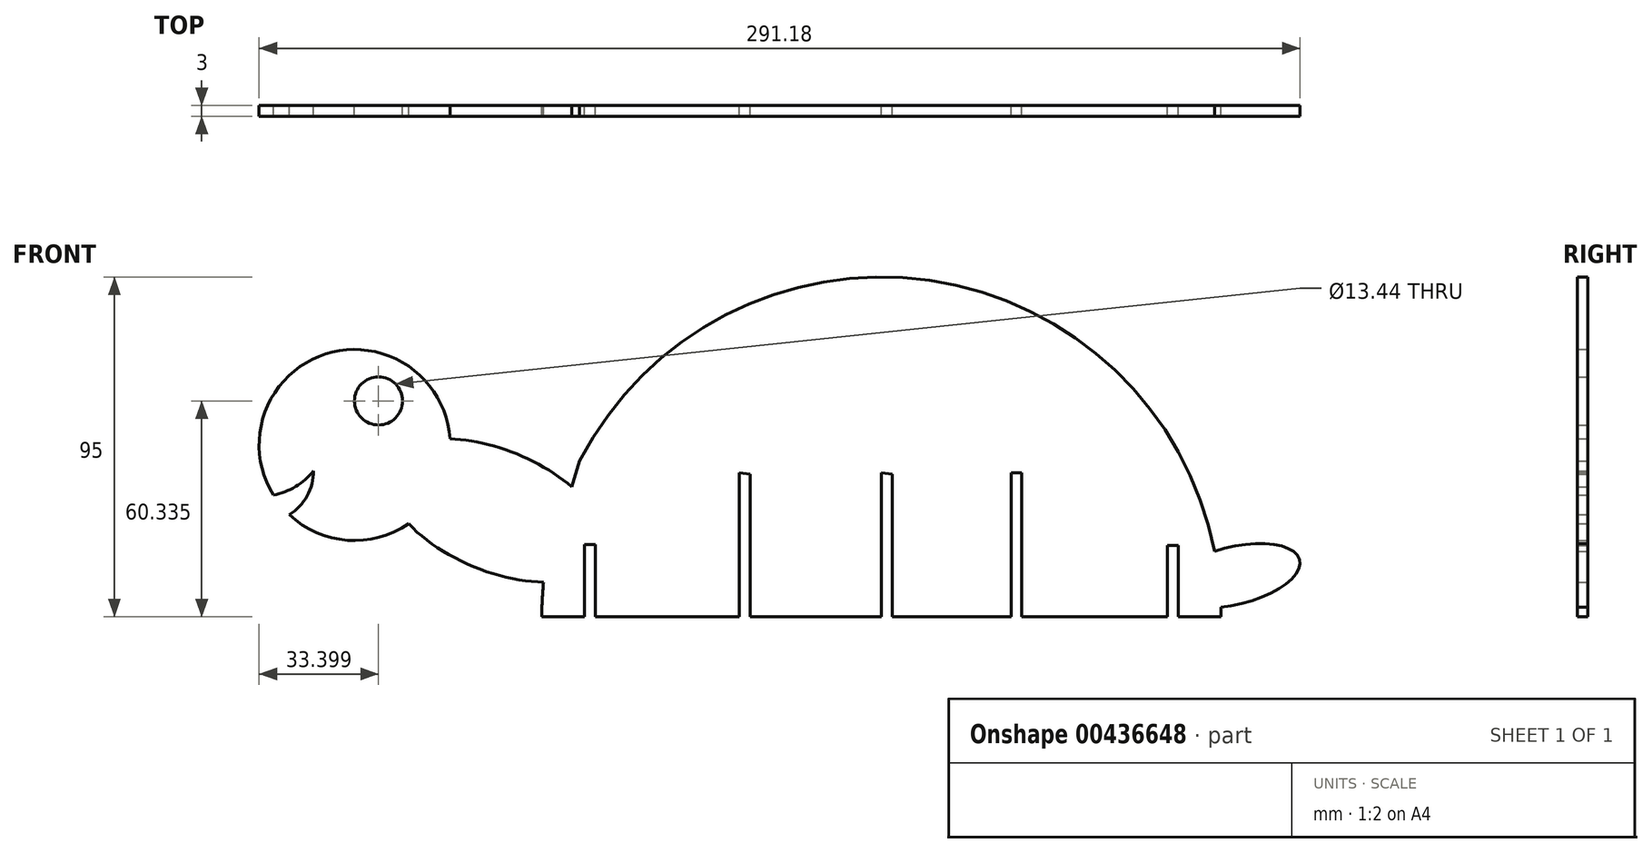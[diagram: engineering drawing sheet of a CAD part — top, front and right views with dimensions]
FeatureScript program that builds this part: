
annotation { "Feature Type Name" : "Feature", "Feature Type Description" : "" }
export const myFeature = defineFeature(function(context is Context, id is Id, definition is map)
    precondition{}
    {
        {
            var Q0;
            Q0=qCreatedBy(makeId("Front.planeOp"),FACE);
            var sketch = newSketch(context, id + "F0", { "sketchPlane" : qUnion([Q0])});
            skLineSegment(sketch, "E0", {"start": v(100.32, 0) * mm, "end": v(88.32, 0) * mm});
            skArc(sketch, "E1", {"start": v(100.32, 0) * mm, "mid": v(100.3, 1.36) * mm, "end": v(100.28, 2.72) * mm});
            skArc(sketch, "E2.trimOffspring", {"start": v(-89.03, 11.13) * mm, "mid": v(-89.52, 5.57) * mm, "end": v(-89.68, 0) * mm});
            skEllipticalArc(sketch, "E3", {});
            skArc(sketch, "E4.trimOffspring", {"start": v(98.55, 18.26) * mm, "mid": v(18.73, 94.05) * mm, "end": v(-79.1, 43.6) * mm});
            skPoint(sketch, "E5", {"position": v(-100.44, 47.2) * mm});
            skLineSegment(sketch, "E6", {"start": v(-79.1, 43.6) * mm, "end": v(-81.32, 36.3) * mm});
            skEllipticalArc(sketch, "E7", {});
            skArc(sketch, "E8", {"start": v(-115.4, 49.77) * mm, "mid": v(-150.18, 73.47) * mm, "end": v(-164.8, 34) * mm});
            skEllipticalArc(sketch, "E9.trimOffspring", {});
            skCircle(sketch, "E10", {"center": v(-135.37, 60.34) * mm, "radius": 6.72 * mm});
            skLineSegment(sketch, "E11", {"start": v(-89.68, 0) * mm, "end": v(-77.68, 0) * mm});
            skLineSegment(sketch, "E12", {"start": v(-74.68, 0) * mm, "end": v(-34.4, 0) * mm});
            skLineSegment(sketch, "E13", {"start": v(85.32, 0) * mm, "end": v(44.6, 0) * mm});
            skLineSegment(sketch, "E14", {"start": v(41.6, 0) * mm, "end": v(8.32, 0) * mm});
            skLineSegment(sketch, "E15", {"start": v(5.32, 0) * mm, "end": v(-31.4, 0) * mm});
            skLineSegment(sketch, "E16", {"start": v(-74.68, 0) * mm, "end": v(-74.68, 20.23) * mm});
            skLineSegment(sketch, "E17", {"start": v(85.32, 0) * mm, "end": v(85.32, 19.87) * mm});
            skPoint(sketch, "E18", {"position": v(-77.68, 0) * mm});
            skLineSegment(sketch, "E19", {"start": v(-77.68, 0) * mm, "end": v(-77.68, 20.23) * mm});
            skLineSegment(sketch, "E20", {"start": v(-77.68, 20.23) * mm, "end": v(-74.68, 20.23) * mm});
            skPoint(sketch, "E21", {"position": v(88.32, 0) * mm});
            skLineSegment(sketch, "E22", {"start": v(88.32, 0) * mm, "end": v(88.32, 19.87) * mm});
            skLineSegment(sketch, "E23", {"start": v(88.32, 19.87) * mm, "end": v(85.32, 19.87) * mm});
            skLineSegment(sketch, "E24", {"start": v(-34.4, 0) * mm, "end": v(-34.4, 40.28) * mm});
            skLineSegment(sketch, "E25", {"start": v(5.32, 0) * mm, "end": v(5.32, 40.28) * mm});
            skLineSegment(sketch, "E26", {"start": v(44.6, 0) * mm, "end": v(44.6, 40.28) * mm});
            skPoint(sketch, "E27", {"position": v(41.6, 0) * mm});
            skLineSegment(sketch, "E28", {"start": v(41.6, 0) * mm, "end": v(41.6, 40.28) * mm});
            skLineSegment(sketch, "E29", {"start": v(41.6, 40.28) * mm, "end": v(44.6, 40.28) * mm});
            skPoint(sketch, "E30", {"position": v(8.32, 0) * mm});
            skLineSegment(sketch, "E31", {"start": v(8.32, 0) * mm, "end": v(8.32, 39.93) * mm});
            skLineSegment(sketch, "E32", {"start": v(8.32, 39.93) * mm, "end": v(5.32, 40.28) * mm});
            skPoint(sketch, "E33", {"position": v(-31.4, 0) * mm});
            skLineSegment(sketch, "E34", {"start": v(-31.4, 0) * mm, "end": v(-31.4, 39.93) * mm});
            skLineSegment(sketch, "E35", {"start": v(-31.4, 39.93) * mm, "end": v(-34.4, 40.28) * mm});
            skLineSegment(sketch, "E36.trimOffspring", {"start": v(-34.4, 0) * mm, "end": v(-74.68, 0) * mm});
            skLineSegment(sketch, "E37.trimOffspring", {"start": v(-77.68, 0) * mm, "end": v(-89.68, 0) * mm});
            skArc(sketch, "E38", {"start": v(-164.8, 34) * mm, "mid": v(-158.26, 36.6) * mm, "end": v(-153.12, 41.39) * mm});
            skArc(sketch, "E39.trimOffspring", {"start": v(-160.33, 28.54) * mm, "mid": v(-144.1, 21.38) * mm, "end": v(-126.95, 25.99) * mm});
            skArc(sketch, "E40", {"start": v(-160.33, 28.54) * mm, "mid": v(-155.33, 33.78) * mm, "end": v(-153.56, 40.8) * mm});
            const initialGuessF0  = {"E3": [0.10418568551540375, 0.011512231081724167, 0.9728062168298889, 0.23162051829904706, 0.018638617259337326, 0.008055484397385654, 4.393831366726673, 1.7828546852865044], "E7": [-0.10265056788921356, 0.029725544154644012, 0.9208176430315056, -0.38999342081874006, 0.032477638261886654, 0.016887533074783013, 4.0125769571110785, 5.3843103583524945], "E9.trimOffspring": [-0.10265056788921356, 0.029725544154644012, 0.9208176430315056, -0.38999342081874006, 0.032477638261886654, 0.016887533074783013, 1.017170301926875, 2.216950804548891]};
            skSetInitialGuess(sketch, initialGuessF0);
            skSolve(sketch);
        }
        {
            var Q0;
            Q0 = qSketchRegion(id + "F0", true);
            extrude(context, id + "F1", {"entities" : qUnion([Q0]), "depth" : 3 * mm, "offsetDistance" : 25 * mm});
        }
    });
